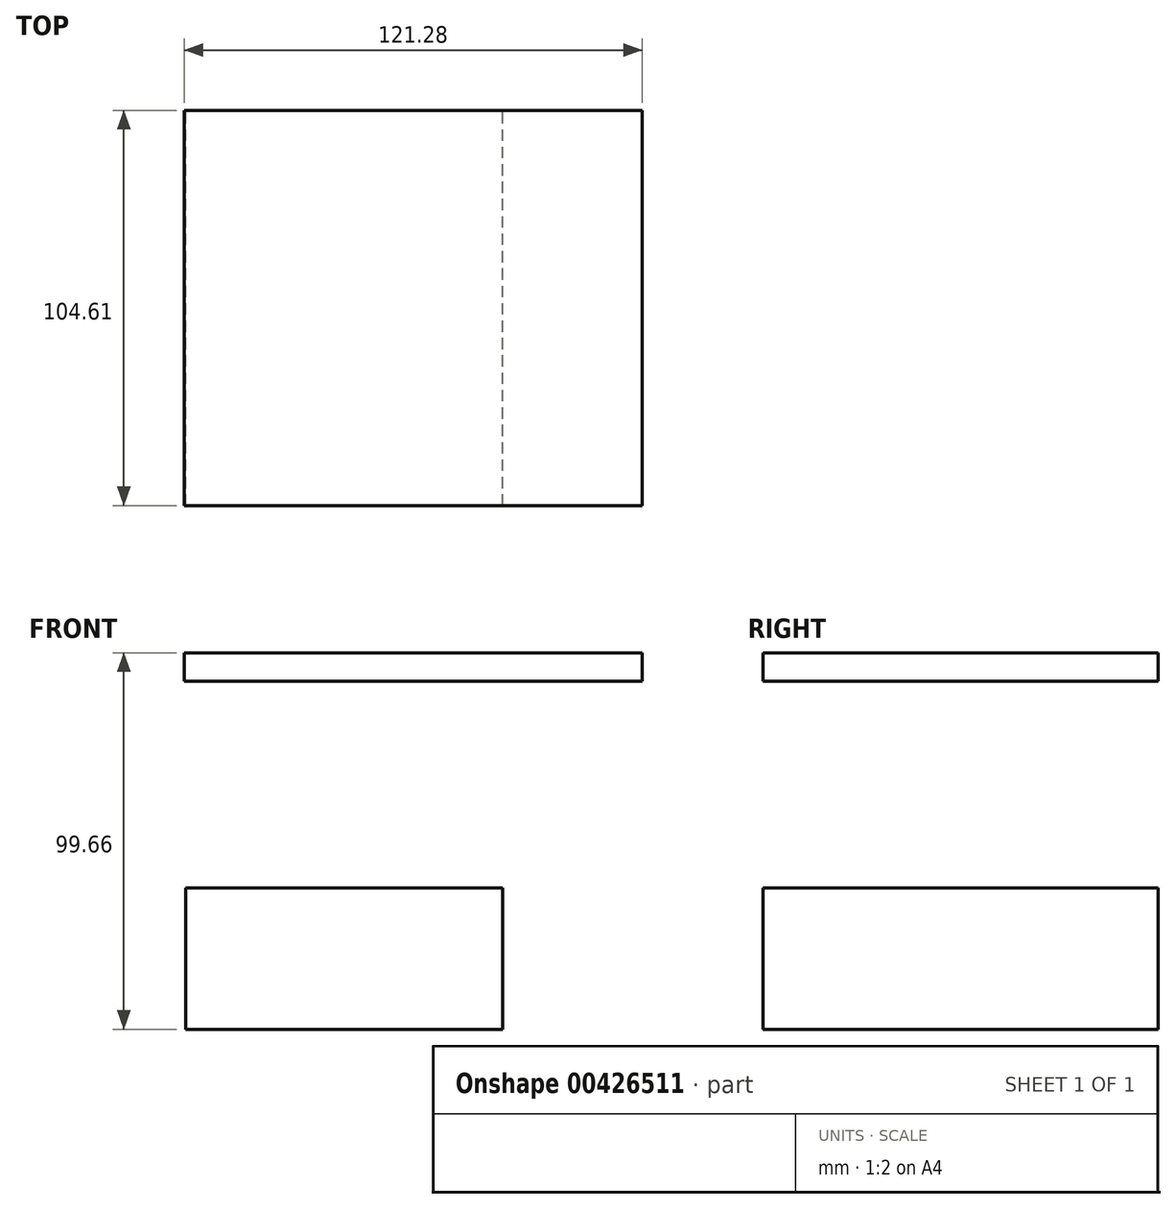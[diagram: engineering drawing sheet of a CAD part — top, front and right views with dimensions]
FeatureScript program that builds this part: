
annotation { "Feature Type Name" : "Feature", "Feature Type Description" : "" }
export const myFeature = defineFeature(function(context is Context, id is Id, definition is map)
    precondition{}
    {
        {
            var Q0;
            Q0=qCreatedBy(makeId("Front.planeOp"),FACE);
            var sketch = newSketch(context, id + "F0", { "sketchPlane" : qUnion([Q0])});
            skLineSegment(sketch, "E0.bottom", {"start": v(60.2, 39.21) * mm, "end": v(-61.08, 39.21) * mm});
            skLineSegment(sketch, "E0.top", {"start": v(60.2, 31.69) * mm, "end": v(-61.08, 31.69) * mm});
            skLineSegment(sketch, "E0.left", {"start": v(60.2, 39.21) * mm, "end": v(60.2, 31.69) * mm});
            skLineSegment(sketch, "E0.right", {"start": v(-61.08, 39.21) * mm, "end": v(-61.08, 31.69) * mm});
            skLineSegment(sketch, "E1.bottom", {"start": v(-60.68, -60.45) * mm, "end": v(23.24, -60.45) * mm});
            skLineSegment(sketch, "E1.top", {"start": v(-60.68, -23.1) * mm, "end": v(23.24, -23.1) * mm});
            skLineSegment(sketch, "E1.left", {"start": v(-60.68, -60.45) * mm, "end": v(-60.68, -23.1) * mm});
            skLineSegment(sketch, "E1.right", {"start": v(23.24, -60.45) * mm, "end": v(23.24, -23.1) * mm});
            skSolve(sketch);
        }
        {
            var Q0;
            Q0 = qSketchRegion(id + "F0", true);
            extrude(context, id + "F1", {"entities" : qUnion([Q0]), "depth" : 104.61 * mm});
        }
    });
